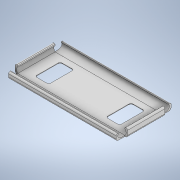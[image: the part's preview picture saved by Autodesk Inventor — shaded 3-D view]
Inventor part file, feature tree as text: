
AUTODESK INVENTOR PART (.ipt)
format: ipt  version: 2020 (Build 240168000, 168)  size: 315,904 bytes
history: native  units: mm
features: sketch x4, extrude x4, fillet x2
ambient origin geometry x8: Origin, YZ Plane, XZ Plane, XY Plane, X Axis, Y Axis, Z Axis, Center Point
bodies: Body1 (feature_tree)
feature tree (10):
  sketch  "Sketch1"  dims[d0=9.5mm d1=11.770907mm]
  sketch  "Sketch2"  dims[d2=50.25602mm d3=63.323636mm]
  extrude  "Extrusion2"  Depth=11.770907mm
  extrude  "Extrusion3"  Depth=63.323636mm
  extrude  "Extrusion4"  Depth=7.278553mm
  extrude  "Extrusion5"  Depth=460.0mm
  fillet  "Fillet1"  Radius=3.006362mm
  fillet  "Fillet2"  Radius=0.381374mm
  sketch  "Sketch3"  dims[d4=7.543377mm d5=7.278553mm]
  sketch  "Sketch4"  dims[d6=13.530576mm d7=10.178962mm d8=3.006362mm d9=0.381374mm d10=8.152475mm d11=90.0deg d12=90.0deg d13=182.762823mm d14=213.345323mm d15=82.749834mm d16=838.251776mm d17=23.985455mm d18=5.035479mm d19=70.066536mm d20=146.705902mm d21=189.528499mm d22=164.68023mm d23=138.415323mm d24=527.101779mm d25=255.80879mm d26=252.614765mm d27=215.951781mm d28=299.08508mm d31=30.0mm d32=33.429929mm d33=50.290385mm d34=63.798039mm d35=8.713599mm d36=18.996342mm d37=3.705985mm d38=4.3568mm d39=21.494574mm d40=1.207753mm d41=4.3568mm d42=7.886471mm d43=0.827129mm d44=4.3568mm d45=1.724373mm d46=6.989226mm d47=3.990886mm d48=12.704485mm d49=3.182814mm d50=11.896413mm d51=20.064763mm d52=3764.948058mm d53=16.37444mm d54=3289.717798mm d55=57.303624mm d56=2466.944268mm d57=59.093716mm d58=46.781222mm d59=3049.802442mm d60=59.093716mm d61=26.771897mm d62=3395.170192mm d63=59.093716mm d64=58.821879mm d65=3579.956247mm d66=158.18518mm d67=2606.435143mm d68=239.777909mm d69=195.409915mm d70=2853.836078mm d71=3289.717798mm d72=16.37444mm d73=3256.109492mm d74=3256.109492mm d75=45.25763mm d76=220.265324mm d77=3276.809698mm d78=3312.698463mm d79=3281.475519mm d80=153.35556mm d81=3202.045193mm d82=1535.478941mm d83=30.0mm d84=0.0mm d85=3600.0mm d86=0.0mm d87=1250.0mm d88=0.0mm d90=420.0mm d91=420.0mm d92=460.0mm d93=471.0mm d94=1200.0mm d95=0.0mm d96=63.5mm d97=15.0mm d98=956.474029mm d99=956.474029mm d100=460.0mm d109=0.5mm d110=0.872665mm d111=0.5mm d112=0.872665mm]
